# Revit family: Shower-Rainhead-KOHLER-Modern-K-22456T
name_source: partatom
category: Plumbing Fixtures
units: mm (PartAtom-declared; Revit-internal decimal feet)

## family parameters
Cut with Voids When Loaded = No
Host = Face
Maintain Annotation Orientation = No
OmniClass Number = 23.31.17.00
OmniClass Title = Showers
Part Type = Normal
Room Calculation Point = No
Round Connector Dimension = Use Diameter
Shared = No

## types (4) — shared parameters
ADA Compliant = No
Assembly Code = D2010700
CW Connection = No
Cold Water Inlet = Cold Water Inlet
Date Modified = 01/09/2025
Default Elevation = 42"
Description = 10 Inch Round Rain Overhead-Plastic
Drain Included = No
Flow Rate = 0 GPM
HW Connection = Yes
Height = 2 1/2"
Hot Water Inlet = Hot Water Inlet
Length = 10"
Manufacturer = Kohler Co.
Master Format 2014 = 22 42 23
Master Format 2014 Name = Residential Showers
Material = Plastic
Panel Thickness = 0"
Pressure = 0.00 psi
Product Documentation Link = https://files.kohler.com.cn
Product Name = Modern
Tempered Water Inlet = Tempered Water Inlet
URL = http://www.kohler.com.cn
Vent Connection = No
Waste Connection = No
Waste Water Outlet = Waste Water Outlet
WaterSense Certified = No
Width = 10"

## per-type parameters (varying)
| type | Finish | Model | Product Page URL | Type |
| BL-Matte Black | Kohler-Plastic-BL-Matte_Black | K-22456T-BL |  | 1 |
| L, BL-Matte Black | Kohler-Plastic-BL-Matte_Black | K-22456T-L-BL |  | 2 |
| L, CP-Polished Chrome | Kohler-Plastic-CP-Polished_Chrome | K-22456T-L-CP | https://www.kohler.com.cn | 3 |
| L, LBN-Non Pvd Brushed Nickel | KOHLER-Plastic-LBN-Non_Pvd_Brushed_Nickel | K-22456T-L-LBN |  | 4 |

## geometry (parser evidence)
native form markers: Sweep x8
no freeform markers — native parametric forms only
